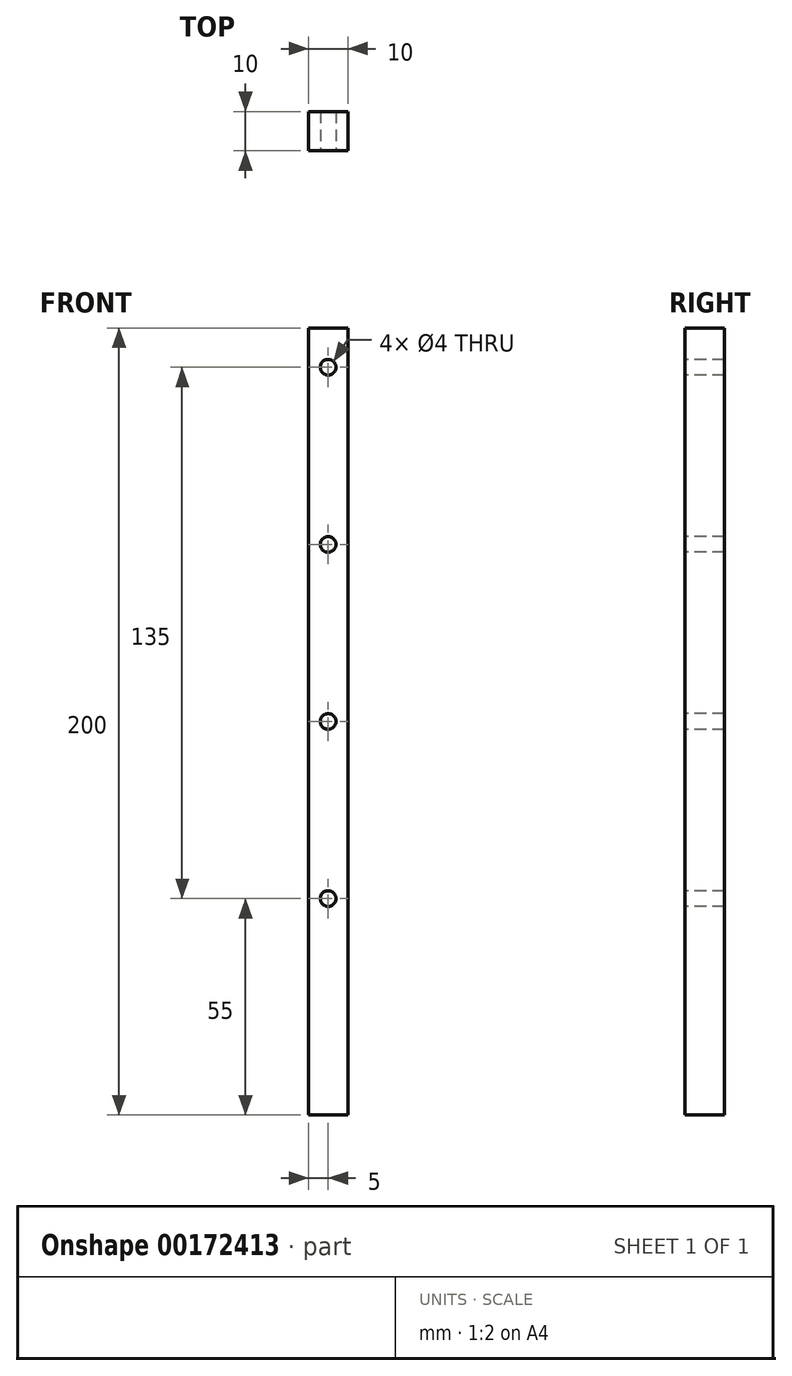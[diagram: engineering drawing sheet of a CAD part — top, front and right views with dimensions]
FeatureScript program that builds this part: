
annotation { "Feature Type Name" : "Feature", "Feature Type Description" : "" }
export const myFeature = defineFeature(function(context is Context, id is Id, definition is map)
    precondition{}
    {
        {
            var Q0;
            Q0=qCreatedBy(makeId("Front.planeOp"),FACE);
            var sketch = newSketch(context, id + "F0", { "sketchPlane" : qUnion([Q0])});
            skLineSegment(sketch, "E0.bottom", {"start": v(0, 0) * mm, "end": v(10, 0) * mm});
            skLineSegment(sketch, "E0.top", {"start": v(0, 200) * mm, "end": v(10, 200) * mm});
            skLineSegment(sketch, "E0.left", {"start": v(0, 0) * mm, "end": v(0, 200) * mm});
            skLineSegment(sketch, "E0.right", {"start": v(10, 0) * mm, "end": v(10, 200) * mm});
            skSolve(sketch);
        }
        {
            var Q0;
            Q0 = qSketchRegion(id + "F0", true);
            extrude(context, id + "F1", {"entities" : qUnion([Q0]), "depth" : 10 * mm});
        }
        {
            var Q0;
            Q0=makeQuery(id+"F1.opExtrude","CAP_FACE",FACE,{"disambiguationData":[OSD([sQuery(id+"F0.wireOp",EDGE,"E0.bottom"),sQuery(id+"F0.wireOp",EDGE,"E0.top"),sQuery(id+"F0.wireOp",EDGE,"E0.left"),sQuery(id+"F0.wireOp",EDGE,"E0.right")])],"isStart":false});
            var sketch = newSketch(context, id + "F2", { "sketchPlane" : qUnion([Q0])});
            skCircle(sketch, "E1", {"center": v(5, 190) * mm, "radius": 2 * mm});
            skCircle(sketch, "E2.1.0.0", {"center": v(5, 145) * mm, "radius": 2 * mm});
            skLineSegment(sketch, "E2.direction1", {"start": v(5, 190) * mm, "end": v(5, 145) * mm, "construction": true});
            skCircle(sketch, "E3.0.2.0", {"center": v(5, 100) * mm, "radius": 2 * mm});
            skCircle(sketch, "E3.0.3.0", {"center": v(5, 55) * mm, "radius": 2 * mm});
            skSolve(sketch);
        }
        {
            var Q0;
            Q0 = qSketchRegion(id + "F2", true);
            extrude(context, id + "F3", {"entities" : qUnion([Q0]), "operationType" : NewBodyOperationType.REMOVE, "endBound" : BoundingType.THROUGH_ALL, "oppositeDirection" : true, "depth" : 25 * mm});
        }
    });
